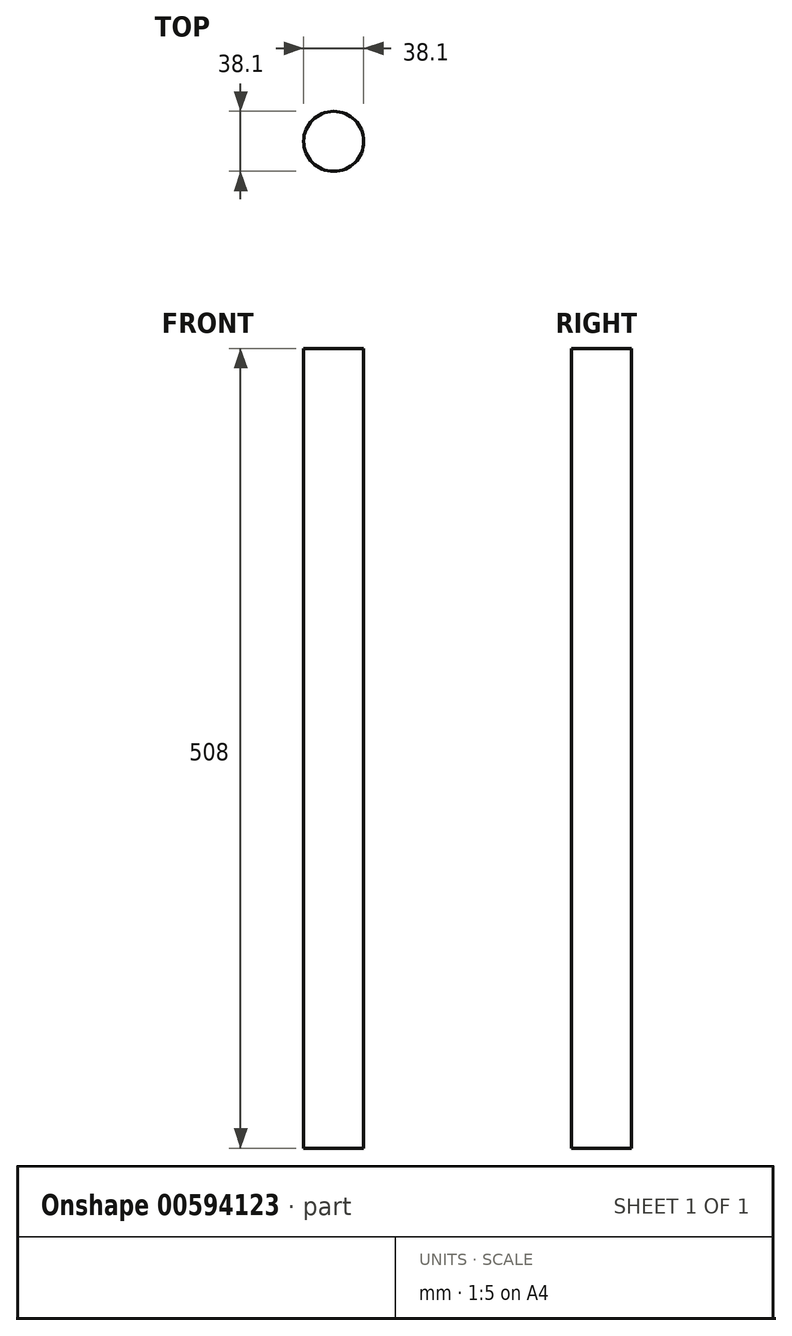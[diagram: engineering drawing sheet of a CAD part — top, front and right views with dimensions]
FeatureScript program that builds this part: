
annotation { "Feature Type Name" : "Feature", "Feature Type Description" : "" }
export const myFeature = defineFeature(function(context is Context, id is Id, definition is map)
    precondition{}
    {
        {
            var Q0;
            Q0=qCreatedBy(makeId("Top.planeOp"),FACE);
            var sketch = newSketch(context, id + "F0", { "sketchPlane" : qUnion([Q0])});
            skCircle(sketch, "E0", {"center": v(0, 0) * mm, "radius": 19.05 * mm});
            skSolve(sketch);
        }
        {
            var Q0;
            Q0 = qSketchRegion(id + "F0", true);
            extrude(context, id + "F1", {"entities" : qUnion([Q0]), "depth" : 508 * mm, "offsetDistance" : 25.4 * mm});
        }
    });
